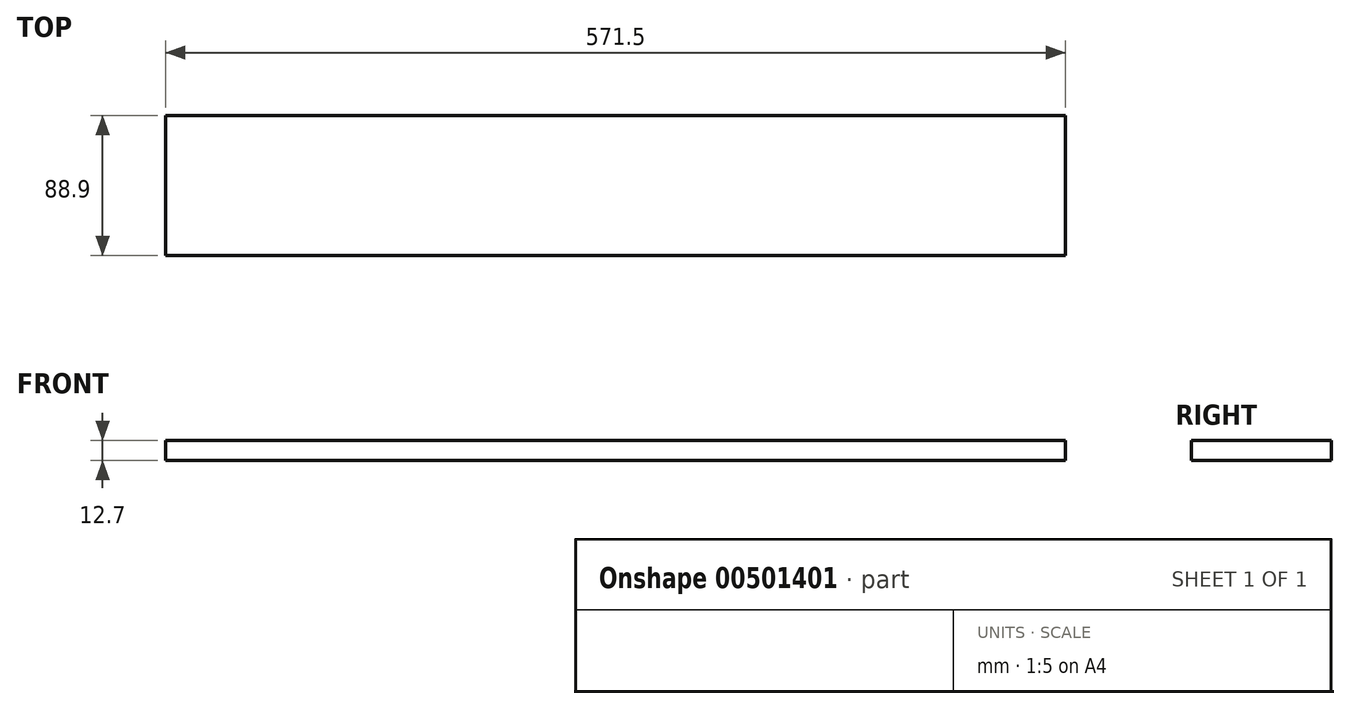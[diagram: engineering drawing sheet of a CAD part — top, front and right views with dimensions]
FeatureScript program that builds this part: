
annotation { "Feature Type Name" : "Feature", "Feature Type Description" : "" }
export const myFeature = defineFeature(function(context is Context, id is Id, definition is map)
    precondition{}
    {
        {
            var Q0;
            Q0=qCreatedBy(makeId("Top.planeOp"),FACE);
            var sketch = newSketch(context, id + "F0", { "sketchPlane" : qUnion([Q0])});
            skLineSegment(sketch, "E0.bottom", {"start": v(0, 0) * mm, "end": v(571.5, 0) * mm});
            skLineSegment(sketch, "E0.top", {"start": v(0, 88.9) * mm, "end": v(571.5, 88.9) * mm});
            skLineSegment(sketch, "E0.left", {"start": v(0, 0) * mm, "end": v(0, 88.9) * mm});
            skLineSegment(sketch, "E0.right", {"start": v(571.5, 0) * mm, "end": v(571.5, 88.9) * mm});
            skSolve(sketch);
        }
        {
            var Q0;
            Q0 = qSketchRegion(id + "F0", true);
            extrude(context, id + "F1", {"entities" : qUnion([Q0]), "depth" : 12.7 * mm});
        }
    });
